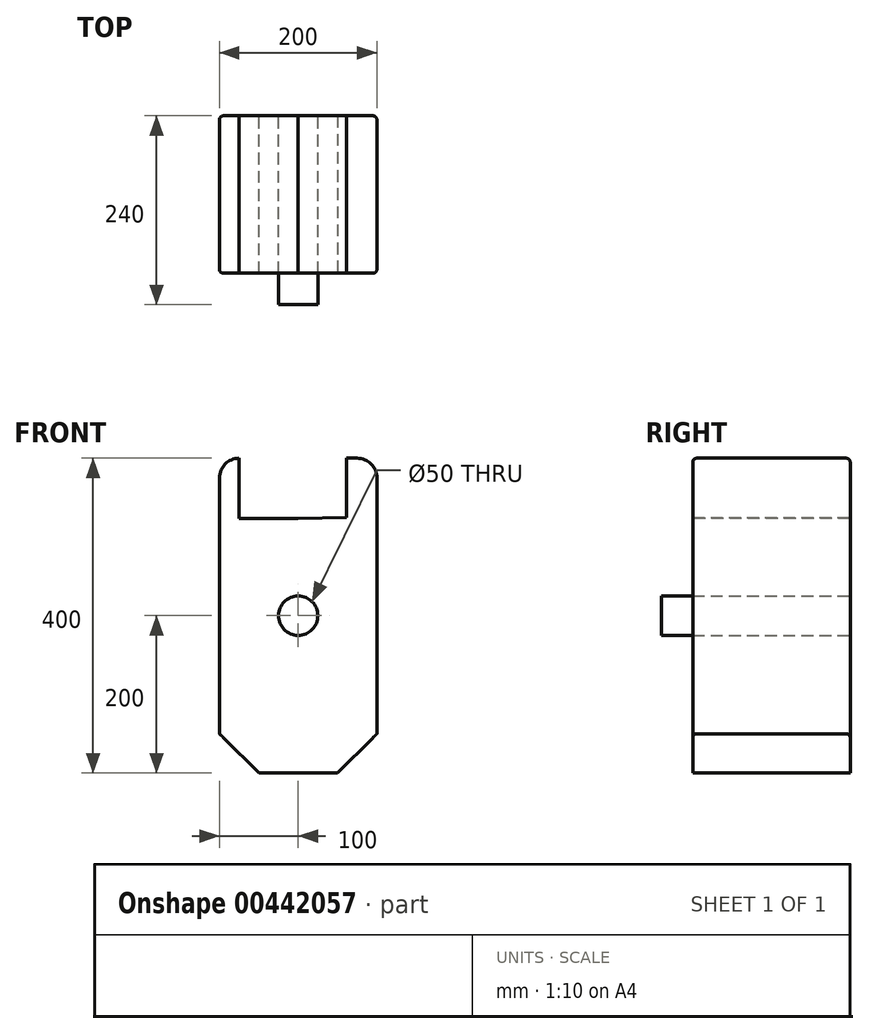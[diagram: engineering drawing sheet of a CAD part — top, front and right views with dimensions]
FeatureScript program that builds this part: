
annotation { "Feature Type Name" : "Feature", "Feature Type Description" : "" }
export const myFeature = defineFeature(function(context is Context, id is Id, definition is map)
    precondition{}
    {
        {
            var Q0;
            Q0=qCreatedBy(makeId("Front.planeOp"),FACE);
            var sketch = newSketch(context, id + "F0", { "sketchPlane" : qUnion([Q0])});
            skLineSegment(sketch, "E0.bottom", {"start": v(75, 200) * mm, "end": v(-75, 200) * mm});
            skLineSegment(sketch, "E0.top", {"start": v(100, -200) * mm, "end": v(-100, -200) * mm});
            skLineSegment(sketch, "E0.left", {"start": v(100, 175) * mm, "end": v(100, -200) * mm});
            skLineSegment(sketch, "E0.right", {"start": v(-100, 175) * mm, "end": v(-100, -200) * mm});
            skPoint(sketch, "E0.middle", {"position": v(0, 0) * mm});
            skPoint(sketch, "E1.visualSharp", {"position": v(-100, 200) * mm});
            skArc(sketch, "E1.filletArc", {"start": v(-75, 200) * mm, "mid": v(-92.68, 192.68) * mm, "end": v(-100, 175) * mm});
            skPoint(sketch, "E2.visualSharp", {"position": v(100, 200) * mm});
            skArc(sketch, "E2.filletArc", {"start": v(100, 175) * mm, "mid": v(92.68, 192.68) * mm, "end": v(75, 200) * mm});
            skCircle(sketch, "E3", {"center": v(0, 0) * mm, "radius": 25 * mm});
            skSolve(sketch);
        }
        {
            var Q0;
            Q0 = qSketchRegion(id + "F0", true);
            extrude(context, id + "F1", {"entities" : qUnion([Q0]), "depth" : 200 * mm});
        }
        {
            var Q0;
            Q0=makeQuery(id+"F1.opExtrude","SWEPT_EDGE",EDGE,{"disambiguationData":[OSD([sQuery(id+"F0.wireOp",EDGE,"E0.top"),sQuery(id+"F0.wireOp",EDGE,"E0.left")])]});
            var Q1;
            Q1=makeQuery(id+"F1.opExtrude","SWEPT_EDGE",EDGE,{"disambiguationData":[OSD([sQuery(id+"F0.wireOp",EDGE,"E0.top"),sQuery(id+"F0.wireOp",EDGE,"E0.right")])]});
            chamfer(context, id + "F2", {"entities" : qUnion([Q0, Q1]), "width" : 50 * mm, "tangentPropagation" : true});
        }
        {
            var Q0;
            Q0=makeQuery(id+"F1.opExtrude","SWEPT_FACE",FACE,{"disambiguationData":[OSD([sQuery(id+"F0.wireOp",EDGE,"E0.bottom")])]});
            fillet(context, id + "F3", {"entities" : qUnion([Q0]), "radius" : 5 * mm, "tangentPropagation" : true, "allowEdgeOverflow" : false});
        }
        {
            var Q0;
            Q0=makeQuery(id+"F1.opExtrude","CAP_FACE",FACE,{"disambiguationData":[OSD([sQuery(id+"F0.wireOp",EDGE,"E0.bottom"),sQuery(id+"F0.wireOp",EDGE,"E0.top"),sQuery(id+"F0.wireOp",EDGE,"E0.left"),sQuery(id+"F0.wireOp",EDGE,"E0.right"),sQuery(id+"F0.wireOp",EDGE,"E1.filletArc"),sQuery(id+"F0.wireOp",EDGE,"E2.filletArc"),sQuery(id+"F0.wireOp",EDGE,"E3")])],"isStart":false});
            var sketch = newSketch(context, id + "F4", { "sketchPlane" : qUnion([Q0])});
            skSolve(sketch);
        }
        {
            var Q0;
            Q0=makeQuery(id+"F4.imprint","IMPRINT",FACE,{"disambiguationData":[TD([[makeQuery(id+"F4.imprint","IMPRINT",EDGE,{"derivedFrom":makeQuery(id+"F1.opExtrude","CAP_EDGE",EDGE,{"disambiguationData":[OSD([sQuery(id+"F0.wireOp",EDGE,"E3")])],"isStart":false})}),1.0]])]});
            extrude(context, id + "F5", {"entities" : qUnion([Q0]), "depth" : 40 * mm, "offsetDistance" : 25 * mm});
        }
        {
            var Q0;
            Q0=makeQuery(id+"F1.opExtrude","CAP_FACE",FACE,{"disambiguationData":[OSD([sQuery(id+"F0.wireOp",EDGE,"E0.bottom"),sQuery(id+"F0.wireOp",EDGE,"E0.top"),sQuery(id+"F0.wireOp",EDGE,"E0.left"),sQuery(id+"F0.wireOp",EDGE,"E0.right"),sQuery(id+"F0.wireOp",EDGE,"E1.filletArc"),sQuery(id+"F0.wireOp",EDGE,"E2.filletArc"),sQuery(id+"F0.wireOp",EDGE,"E3")])],"isStart":false});
            var sketch = newSketch(context, id + "F6", { "sketchPlane" : qUnion([Q0])});
            skLineSegment(sketch, "E4", {"start": v(-75, 195) * mm, "end": v(-75, 123.5) * mm});
            skLineSegment(sketch, "E5", {"start": v(-75, 123.5) * mm, "end": v(0, 123.5) * mm});
            skLineSegment(sketch, "E6", {"start": v(0, 123.5) * mm, "end": v(0, 213.13) * mm});
            skLineSegment(sketch, "E7", {"start": v(0, 213.13) * mm, "end": v(-75, 213.13) * mm});
            skLineSegment(sketch, "E8", {"start": v(-75, 213.13) * mm, "end": v(-75, 195) * mm});
            skSolve(sketch);
        }
        {
            var Q0;
            Q0 = qSketchRegion(id + "F6", true);
            var Q1;
            Q1=makeQuery(id+"F1.opExtrude","CAP_FACE",FACE,{"disambiguationData":[OSD([sQuery(id+"F0.wireOp",EDGE,"E0.bottom"),sQuery(id+"F0.wireOp",EDGE,"E0.top"),sQuery(id+"F0.wireOp",EDGE,"E0.left"),sQuery(id+"F0.wireOp",EDGE,"E0.right"),sQuery(id+"F0.wireOp",EDGE,"E1.filletArc"),sQuery(id+"F0.wireOp",EDGE,"E2.filletArc"),sQuery(id+"F0.wireOp",EDGE,"E3")])],"isStart":true});
            extrude(context, id + "F7", {"entities" : qUnion([Q0, Q1]), "operationType" : NewBodyOperationType.REMOVE, "oppositeDirection" : true, "depth" : 5025 * mm, "offsetDistance" : 25 * mm});
        }
        {
            var Q0;
            Q0=makeQuery(id+"F1.opExtrude","CAP_FACE",FACE,{"disambiguationData":[OSD([sQuery(id+"F0.wireOp",EDGE,"E0.bottom"),sQuery(id+"F0.wireOp",EDGE,"E0.top"),sQuery(id+"F0.wireOp",EDGE,"E0.left"),sQuery(id+"F0.wireOp",EDGE,"E0.right"),sQuery(id+"F0.wireOp",EDGE,"E1.filletArc"),sQuery(id+"F0.wireOp",EDGE,"E2.filletArc"),sQuery(id+"F0.wireOp",EDGE,"E3")])],"isStart":true});
            var sketch = newSketch(context, id + "F8", { "sketchPlane" : qUnion([Q0])});
            skLineSegment(sketch, "E9", {"start": v(-61.08, 195) * mm, "end": v(-61.08, 124.8) * mm});
            skLineSegment(sketch, "E10", {"start": v(-61.08, 124.8) * mm, "end": v(0, 123.5) * mm});
            skLineSegment(sketch, "E11", {"start": v(0, 123.5) * mm, "end": v(0, 195) * mm});
            skLineSegment(sketch, "E12", {"start": v(0, 195) * mm, "end": v(-61.08, 195) * mm});
            skSolve(sketch);
        }
        {
            var Q0;
            Q0=makeQuery(id+"F8.imprint","IMPRINT",FACE,{"disambiguationData":[TD([[makeQuery(id+"F8.imprint","IMPRINT",EDGE,{"derivedFrom":sQuery(id+"F8.wireOp",EDGE,"E9")}),1.0]])]});
            extrude(context, id + "F9", {"entities" : qUnion([Q0]), "operationType" : NewBodyOperationType.REMOVE, "oppositeDirection" : true, "depth" : 25 * mm, "offsetDistance" : 25 * mm});
        }
        {
            var Q0;
            Q0=makeQuery(id+"F9.boolean.opBoolean","COPY",FACE,{"derivedFrom":makeQuery(id+"F9.opExtrude","CAP_FACE",FACE,{"disambiguationData":[OSD([sQuery(id+"F8.wireOp",EDGE,"E9"),sQuery(id+"F8.wireOp",EDGE,"E10"),sQuery(id+"F8.wireOp",EDGE,"E11"),sQuery(id+"F8.wireOp",EDGE,"E12")])],"isStart":false})});
            extrude(context, id + "F10", {"entities" : qUnion([Q0]), "operationType" : NewBodyOperationType.ADD, "depth" : 450 * mm, "offsetDistance" : 25 * mm});
        }
        {
            var Q0;
            Q0=makeQuery(id+"F10.opExtrude","CAP_FACE",FACE,{"disambiguationData":[OSD([sQuery(id+"F8.wireOp",EDGE,"E9"),sQuery(id+"F8.wireOp",EDGE,"E10"),sQuery(id+"F8.wireOp",EDGE,"E11"),sQuery(id+"F8.wireOp",EDGE,"E12")])],"isStart":false});
            extrude(context, id + "F11", {"entities" : qUnion([Q0]), "operationType" : NewBodyOperationType.REMOVE, "oppositeDirection" : true, "depth" : 700 * mm, "offsetDistance" : 25 * mm});
        }
        {
            var Q0;
            Q0=makeQuery(id+"F11.boolean.opBoolean","COPY",FACE,{"derivedFrom":makeQuery(id+"F11.opExtrude","SWEPT_FACE",FACE,{"disambiguationData":[OSD([sQuery(id+"F8.wireOp",EDGE,"E12")])]})});
            extrude(context, id + "F12", {"entities" : qUnion([Q0]), "operationType" : NewBodyOperationType.REMOVE, "oppositeDirection" : true, "depth" : 25 * mm, "offsetDistance" : 25 * mm});
        }
    });
